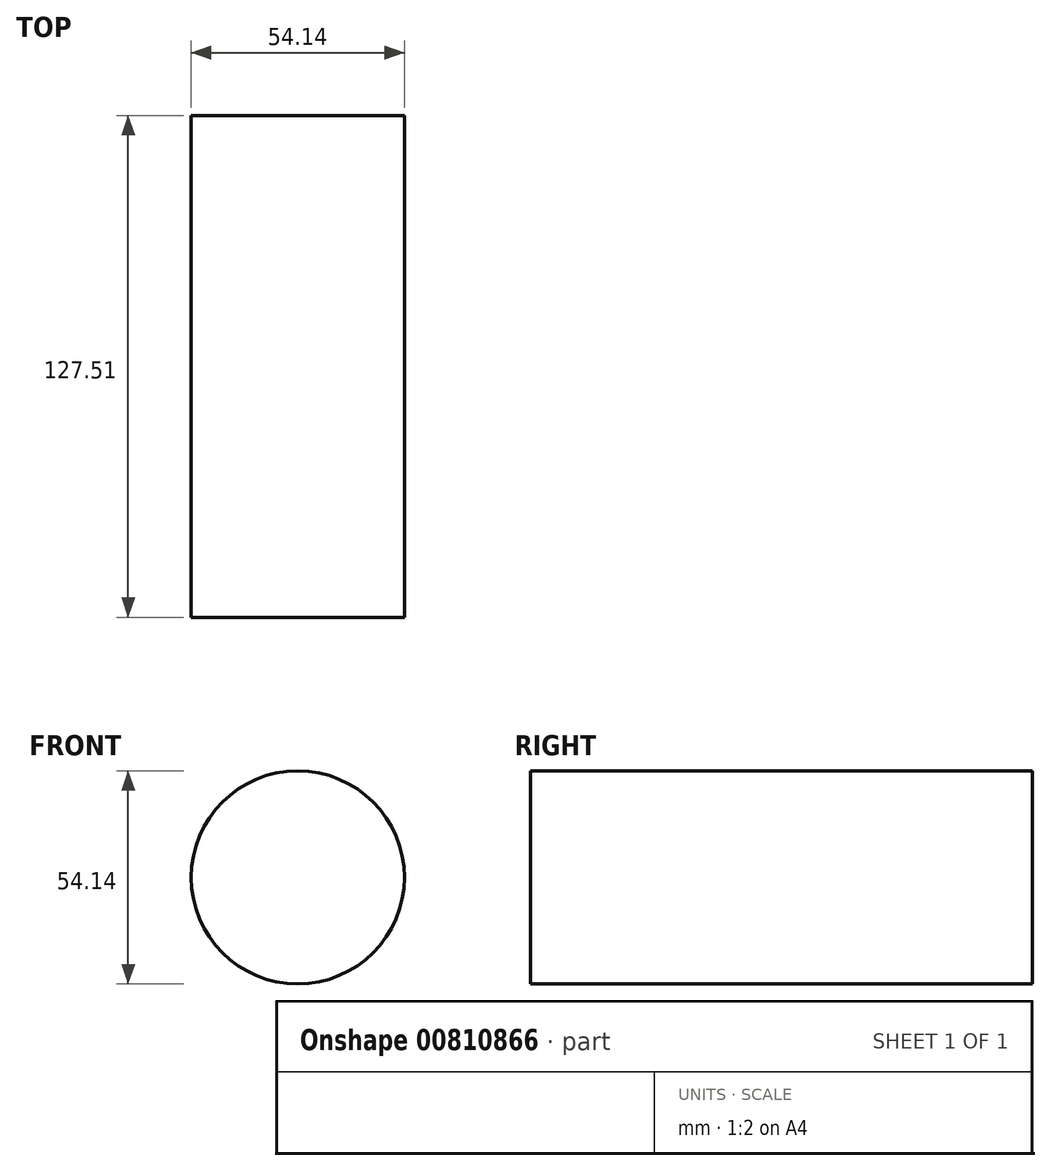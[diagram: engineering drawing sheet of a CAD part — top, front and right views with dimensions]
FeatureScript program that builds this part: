
annotation { "Feature Type Name" : "Feature", "Feature Type Description" : "" }
export const myFeature = defineFeature(function(context is Context, id is Id, definition is map)
    precondition{}
    {
        {
            var Q0;
            Q0=qCreatedBy(makeId("Front.planeOp"),FACE);
            var sketch = newSketch(context, id + "F0", { "sketchPlane" : qUnion([Q0])});
            skCircle(sketch, "E0", {"center": v(0, 0) * mm, "radius": 27.07 * mm});
            skSolve(sketch);
        }
        {
            var Q0;
            Q0=makeQuery(id+"F0.imprint","IMPRINT",FACE,{"disambiguationData":[TD([[makeQuery(id+"F0.imprint","IMPRINT",EDGE,{"derivedFrom":sQuery(id+"F0.wireOp",EDGE,"E0")}),1.0]])]});
            extrude(context, id + "F1", {"entities" : qUnion([Q0]), "depth" : 127.5 * mm, "offsetDistance" : 25.4 * mm});
        }
    });
